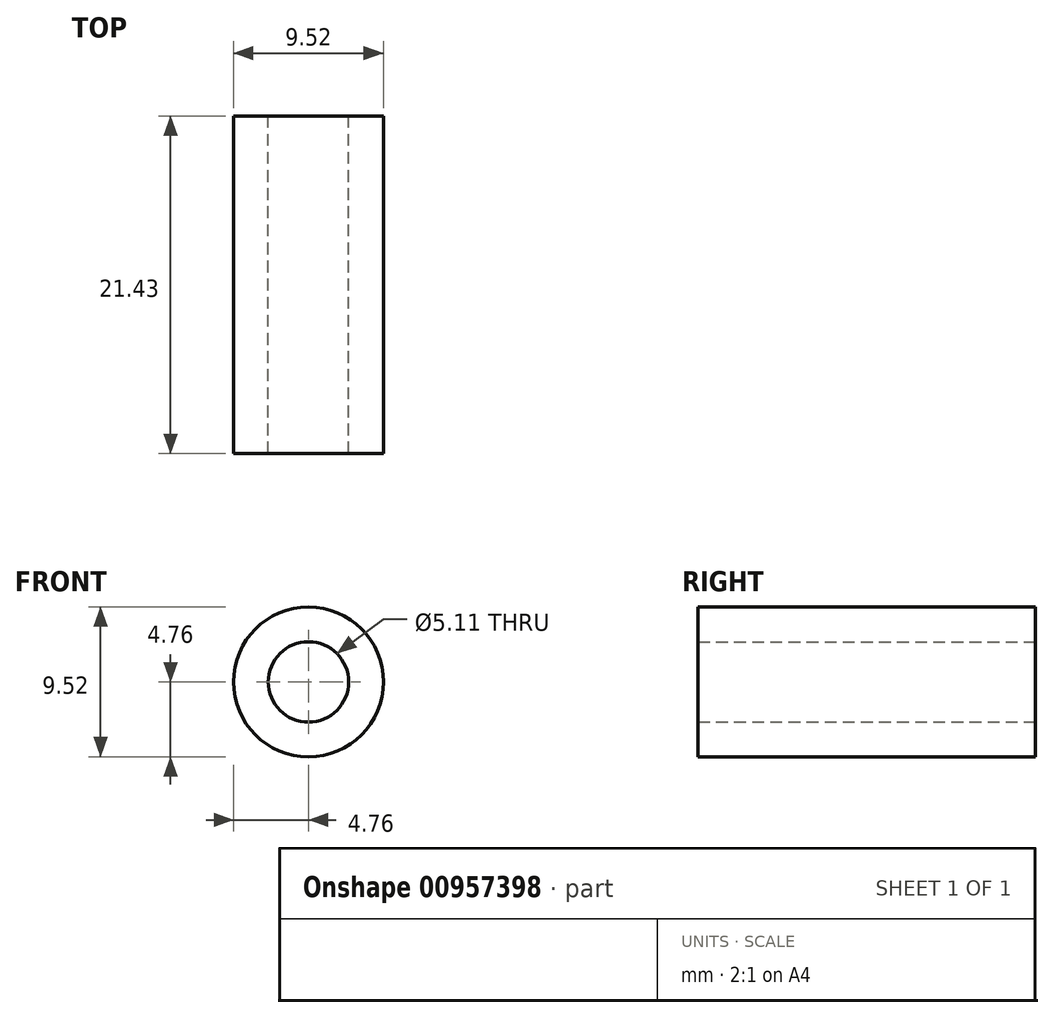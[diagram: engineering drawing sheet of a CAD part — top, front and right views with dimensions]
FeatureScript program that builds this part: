
annotation { "Feature Type Name" : "Feature", "Feature Type Description" : "" }
export const myFeature = defineFeature(function(context is Context, id is Id, definition is map)
    precondition{}
    {
        {
            var Q0;
            Q0=qCreatedBy(makeId("Front.planeOp"),FACE);
            var sketch = newSketch(context, id + "F0", { "sketchPlane" : qUnion([Q0])});
            skCircle(sketch, "E0", {"center": v(0, 0) * mm, "radius": 2.55 * mm});
            skCircle(sketch, "E1", {"center": v(0, 0) * mm, "radius": 4.76 * mm});
            skSolve(sketch);
        }
        {
            var Q0;
            Q0 = qSketchRegion(id + "F0", true);
            extrude(context, id + "F1", {"entities" : qUnion([Q0]), "depth" : 21.43 * mm, "offsetDistance" : 25.4 * mm});
        }
    });
